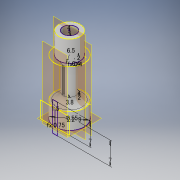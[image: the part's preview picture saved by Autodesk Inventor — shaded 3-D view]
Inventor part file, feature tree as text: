
AUTODESK INVENTOR PART (.ipt)
format: ipt  version: 2019.3 (Build 233278000, 278)  size: 186,368 bytes
history: native  units: in
note: dims shown in document units (in); Inventor stores cm internally (conversion verified against a paired STEP export)
features: sketch x6, extrude x6, other x4, projected_geometry x3, fillet x1
ambient origin geometry x8: Origin, YZ Plane, XZ Plane, XY Plane, X Axis, Y Axis, Z Axis, Center Point
bodies: Body1 (feature_tree)
feature tree (20):
  other  "ソリッド1"
  sketch  "スケッチ2"
  sketch  "スケッチ1"
  extrude  "押し出し1"  Depth=0.0866in
  extrude  "押し出し2"  Depth=0.0217in
  other  "作業平面2"
  sketch  "スケッチ4"
  sketch  "スケッチ3"
  extrude  "押し出し6"  Depth=0.1969in TaperAngle=0.0deg
  other  "作業平面3"
  sketch  "スケッチ5"
  extrude  "押し出し8"  Depth=0.1181in TaperAngle=0.0deg
  sketch  "スケッチ7"
  extrude  "押し出し9"  Depth=0.3543in
  other  "作業平面4"
  extrude  "押し出し10"  Depth=0.1496in
  fillet  "フィレット3"  Radius=0.2756in
  projected_geometry  "投影ループ1"
  projected_geometry  "投影ループ2"
  projected_geometry  "投影ループ3"
